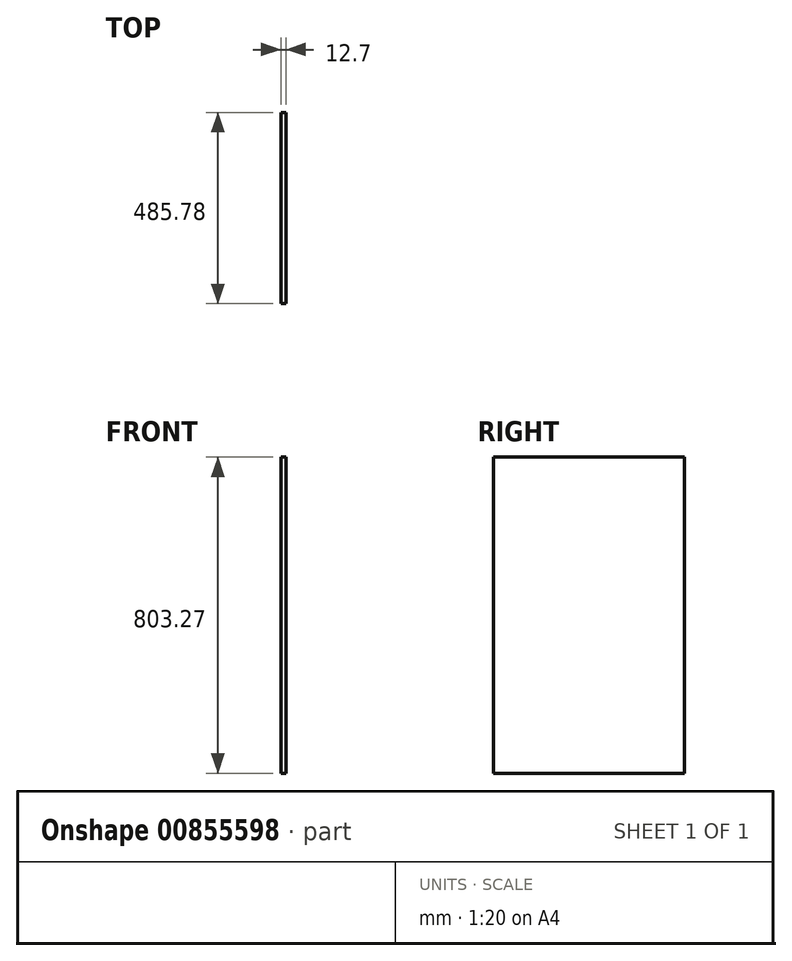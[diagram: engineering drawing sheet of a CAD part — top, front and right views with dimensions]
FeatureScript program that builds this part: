
annotation { "Feature Type Name" : "Feature", "Feature Type Description" : "" }
export const myFeature = defineFeature(function(context is Context, id is Id, definition is map)
    precondition{}
    {
        {
            var Q0;
            Q0=qCreatedBy(makeId("Right.planeOp"),FACE);
            var sketch = newSketch(context, id + "F0", { "sketchPlane" : qUnion([Q0])});
            skLineSegment(sketch, "E0.bottom", {"start": v(0, 0) * mm, "end": v(485.77, 0) * mm});
            skLineSegment(sketch, "E0.top", {"start": v(0, -803.27) * mm, "end": v(485.78, -803.27) * mm});
            skLineSegment(sketch, "E0.left", {"start": v(0, 0) * mm, "end": v(0, -803.27) * mm});
            skLineSegment(sketch, "E0.right", {"start": v(485.78, 0) * mm, "end": v(485.78, -803.27) * mm});
            skSolve(sketch);
        }
        {
            var Q0;
            Q0 = qSketchRegion(id + "F0", true);
            extrude(context, id + "F1", {"entities" : qUnion([Q0]), "depth" : 12.7 * mm, "offsetDistance" : 25.4 * mm});
        }
    });
